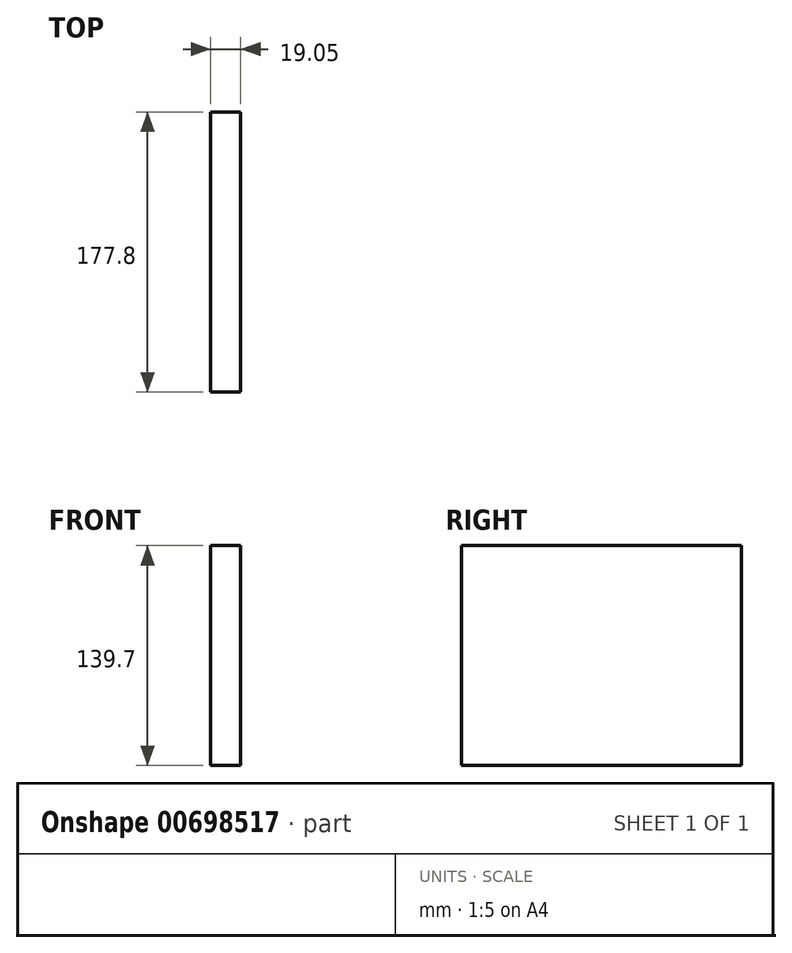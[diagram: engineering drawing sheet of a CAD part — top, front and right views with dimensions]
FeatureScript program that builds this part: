
annotation { "Feature Type Name" : "Feature", "Feature Type Description" : "" }
export const myFeature = defineFeature(function(context is Context, id is Id, definition is map)
    precondition{}
    {
        {
            var Q0;
            Q0=qCreatedBy(makeId("Right.planeOp"),FACE);
            var sketch = newSketch(context, id + "F0", { "sketchPlane" : qUnion([Q0])});
            skLineSegment(sketch, "E0.bottom", {"start": v(-69.4, -78.9) * mm, "end": v(108.4, -78.9) * mm});
            skLineSegment(sketch, "E0.top", {"start": v(-69.4, 60.8) * mm, "end": v(108.4, 60.8) * mm});
            skLineSegment(sketch, "E0.left", {"start": v(-69.4, -78.9) * mm, "end": v(-69.4, 60.8) * mm});
            skLineSegment(sketch, "E0.right", {"start": v(108.4, -78.9) * mm, "end": v(108.4, 60.8) * mm});
            skSolve(sketch);
        }
        {
            var Q0;
            Q0 = qSketchRegion(id + "F0", true);
            extrude(context, id + "F1", {"entities" : qUnion([Q0]), "depth" : 19.05 * mm, "offsetDistance" : 25.4 * mm});
        }
    });
